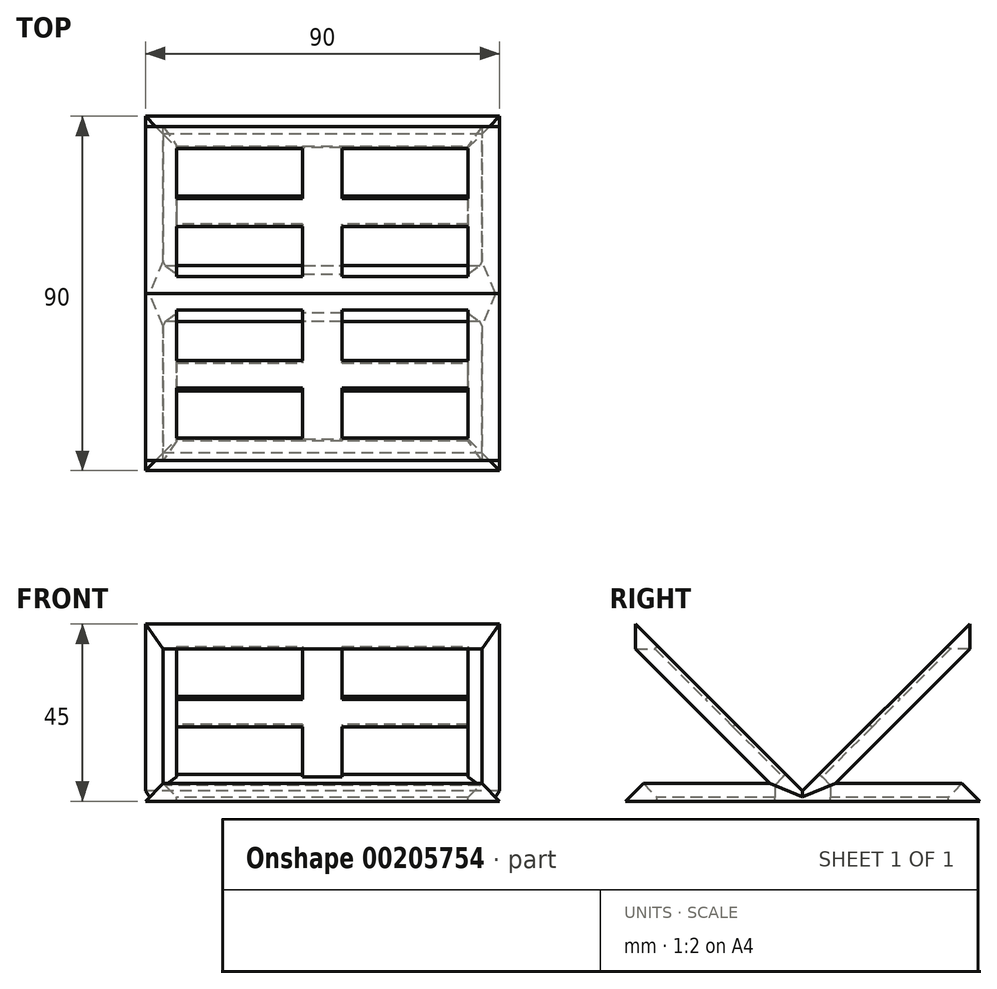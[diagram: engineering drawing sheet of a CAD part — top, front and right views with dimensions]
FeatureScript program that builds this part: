
annotation { "Feature Type Name" : "Feature", "Feature Type Description" : "" }
export const myFeature = defineFeature(function(context is Context, id is Id, definition is map)
    precondition{}
    {
        {
            var Q0;
            Q0=qCreatedBy(makeId("Right.planeOp"),FACE);
            var sketch = newSketch(context, id + "F12", { "sketchPlane" : qUnion([Q0])});
            skLineSegment(sketch, "E0.bottom", {"start": v(-45, 45) * mm, "end": v(45, 45) * mm});
            skLineSegment(sketch, "E0.top", {"start": v(-45, 0) * mm, "end": v(45, 0) * mm});
            skLineSegment(sketch, "E0.left", {"start": v(-45, 45) * mm, "end": v(-45, 0) * mm});
            skLineSegment(sketch, "E0.right", {"start": v(45, 45) * mm, "end": v(45, 0) * mm});
            skLineSegment(sketch, "E1", {"start": v(-42.43, 45) * mm, "end": v(0, 2.57) * mm});
            skLineSegment(sketch, "E2", {"start": v(0, 0) * mm, "end": v(0, 45) * mm, "construction": true});
            skLineSegment(sketch, "E3.MirrorCS", {"start": v(42.43, 45) * mm, "end": v(0, 2.57) * mm});
            skSolve(sketch);
        }
        {
            var Q0;
            Q0=makeQuery(id+"F12.imprint","IMPRINT",FACE,{"disambiguationData":[TD([[makeQuery(id+"F12.imprint","IMPRINT",EDGE,{"derivedFrom":sQuery(id+"F12.wireOp",EDGE,"E0.top")}),1.0]])]});
            extrude(context, id + "F0", {"entities" : qUnion([Q0]), "depth" : 45 * mm});
        }
        {
            var Q0;
            Q0=makeQuery(id+"F0.opExtrude","SWEPT_BODY",BODY,{"disambiguationData":[OSD([sQuery(id+"F12.wireOp",EDGE,"E0.bottom"),sQuery(id+"F12.wireOp",EDGE,"E0.top"),sQuery(id+"F12.wireOp",EDGE,"E0.left"),sQuery(id+"F12.wireOp",EDGE,"E0.right"),sQuery(id+"F12.wireOp",EDGE,"E1"),sQuery(id+"F12.wireOp",EDGE,"E3.MirrorCS")])]});
            var Q1;
            Q1=qCreatedBy(makeId("Right.planeOp"),FACE);
            mirror(context, id + "F1", {"operationType" : NewBodyOperationType.ADD, "entities" : qUnion([Q0]), "mirrorPlane" : qUnion([Q1])});
        }
        {
            var Q0;
            {var subQ0=makeQuery(id+"F0.opExtrude","SWEPT_FACE",FACE,{"disambiguationData":[OSD([sQuery(id+"F12.wireOp",EDGE,"E0.left")])]});Q0=makeQuery(id+"F1.boolean.opBoolean","MERGE",FACE,{"derivedFrom":[subQ0,makeQuery(id+"F1.opPattern","COPY",FACE,{"derivedFrom":subQ0,"instanceName":"1"})]});}
            var Q1;
            {var subQ0=makeQuery(id+"F0.opExtrude","SWEPT_FACE",FACE,{"disambiguationData":[OSD([sQuery(id+"F12.wireOp",EDGE,"E0.right")])]});Q1=makeQuery(id+"F1.boolean.opBoolean","MERGE",FACE,{"derivedFrom":[subQ0,makeQuery(id+"F1.opPattern","COPY",FACE,{"derivedFrom":subQ0,"instanceName":"1"})]});}
            var Q2;
            Q2=makeQuery(id+"F1.opPattern","COPY",FACE,{"derivedFrom":makeQuery(id+"F0.opExtrude","CAP_FACE",FACE,{"disambiguationData":[OSD([sQuery(id+"F12.wireOp",EDGE,"E0.bottom"),sQuery(id+"F12.wireOp",EDGE,"E0.top"),sQuery(id+"F12.wireOp",EDGE,"E0.left"),sQuery(id+"F12.wireOp",EDGE,"E0.right"),sQuery(id+"F12.wireOp",EDGE,"E1"),sQuery(id+"F12.wireOp",EDGE,"E3.MirrorCS")])],"isStart":false}),"instanceName":"1"});
            var Q3;
            Q3=makeQuery(id+"F0.opExtrude","CAP_FACE",FACE,{"disambiguationData":[OSD([sQuery(id+"F12.wireOp",EDGE,"E0.bottom"),sQuery(id+"F12.wireOp",EDGE,"E0.top"),sQuery(id+"F12.wireOp",EDGE,"E0.left"),sQuery(id+"F12.wireOp",EDGE,"E0.right"),sQuery(id+"F12.wireOp",EDGE,"E1"),sQuery(id+"F12.wireOp",EDGE,"E3.MirrorCS")])],"isStart":false});
            shell(context, id + "F2", {"entities" : qUnion([Q0, Q1, Q2, Q3]), "thickness" : 4 * mm});
        }
        {
            var Q0;
            {var subQ0=sQuery(id+"F12.wireOp",EDGE,"E0.bottom");var subQ1=makeQuery(id+"F0.opExtrude","SWEPT_FACE",FACE,{"disambiguationData":[OSD([subQ0]),TDD([makeQuery(id+"F12.imprint","IMPRINT",EDGE,{"disambiguationData":[TD([[makeQuery(id+"F12.imprint","INTERSECT",VERTEX,{"derivedFrom":[subQ0,sQuery(id+"F12.wireOp",EDGE,"E0.right")]}),1.0]])],"derivedFrom":subQ0})])]});Q0=makeQuery(id+"F1.boolean.opBoolean","MERGE",FACE,{"derivedFrom":[subQ1,makeQuery(id+"F1.opPattern","COPY",FACE,{"derivedFrom":subQ1,"instanceName":"1"})]});}
            extrude(context, id + "F13", {"entities" : qUnion([Q0]), "operationType" : NewBodyOperationType.REMOVE, "oppositeDirection" : true, "depth" : 17.8 * mm});
        }
        {
            var Q0;
            {var subQ0=sQuery(id+"F12.wireOp",EDGE,"E0.bottom");var subQ1=makeQuery(id+"F0.opExtrude","SWEPT_FACE",FACE,{"disambiguationData":[OSD([subQ0]),TDD([makeQuery(id+"F12.imprint","IMPRINT",EDGE,{"disambiguationData":[TD([[makeQuery(id+"F12.imprint","INTERSECT",VERTEX,{"derivedFrom":[subQ0,sQuery(id+"F12.wireOp",EDGE,"E0.left")]}),-1.0]])],"derivedFrom":subQ0})])]});Q0=makeQuery(id+"F1.boolean.opBoolean","MERGE",FACE,{"derivedFrom":[subQ1,makeQuery(id+"F1.opPattern","COPY",FACE,{"derivedFrom":subQ1,"instanceName":"1"})]});}
            extrude(context, id + "F3", {"entities" : qUnion([Q0]), "operationType" : NewBodyOperationType.REMOVE, "oppositeDirection" : true, "depth" : 25 * mm});
        }
        {
            var Q0;
            Q0=makeQuery(id+"F0.opExtrude","CAP_FACE",FACE,{"disambiguationData":[OSD([sQuery(id+"F12.wireOp",EDGE,"E0.bottom"),sQuery(id+"F12.wireOp",EDGE,"E0.top"),sQuery(id+"F12.wireOp",EDGE,"E0.left"),sQuery(id+"F12.wireOp",EDGE,"E0.right"),sQuery(id+"F12.wireOp",EDGE,"E1"),sQuery(id+"F12.wireOp",EDGE,"E3.MirrorCS")])],"isStart":false});
            var sketch = newSketch(context, id + "F14", { "sketchPlane" : qUnion([Q0])});
            skLineSegment(sketch, "E4", {"start": v(-45, 0) * mm, "end": v(-41, 4) * mm});
            skLineSegment(sketch, "E5", {"start": v(-41, 4) * mm, "end": v(-45, 4) * mm});
            skLineSegment(sketch, "E6", {"start": v(-45, 4) * mm, "end": v(-45, 0) * mm});
            skLineSegment(sketch, "E7", {"start": v(41, 4) * mm, "end": v(45, 0) * mm});
            skLineSegment(sketch, "E8", {"start": v(41, 4) * mm, "end": v(45, 4) * mm});
            skLineSegment(sketch, "E9", {"start": v(45, 4) * mm, "end": v(45, 4) * mm});
            skLineSegment(sketch, "E10", {"start": v(45, 0) * mm, "end": v(45, 4) * mm});
            skSolve(sketch);
        }
        {
            var Q0;
            Q0 = qSketchRegion(id + "F14", true);
            extrude(context, id + "F15", {"entities" : qUnion([Q0]), "operationType" : NewBodyOperationType.REMOVE, "endBound" : BoundingType.THROUGH_ALL, "oppositeDirection" : true, "depth" : 25 * mm});
        }
        {
            var Q0;
            {var subQ0=sQuery(id+"F12.wireOp",EDGE,"E1");Q0=makeQuery(id+"F2.opShell","OFFSET_EDGE",EDGE,{"disambiguationData":[OSD([subQ0]),TDD([makeQuery(id+"F0.opExtrude","CAP_EDGE",EDGE,{"disambiguationData":[OSD([subQ0])],"isStart":false})])]});}
            var Q1;
            {var subQ0=sQuery(id+"F12.wireOp",EDGE,"E1");Q1=makeQuery(id+"F2.opShell","OFFSET_EDGE",EDGE,{"disambiguationData":[OSD([subQ0]),TDD([makeQuery(id+"F1.opPattern","COPY",EDGE,{"derivedFrom":makeQuery(id+"F0.opExtrude","CAP_EDGE",EDGE,{"disambiguationData":[OSD([subQ0])],"isStart":false}),"instanceName":"1"})])]});}
            var Q2;
            {var subQ0=sQuery(id+"F12.wireOp",EDGE,"E0.top");Q2=makeQuery(id+"F2.opShell","OFFSET_EDGE",EDGE,{"disambiguationData":[OSD([subQ0]),TDD([makeQuery(id+"F1.opPattern","COPY",EDGE,{"derivedFrom":makeQuery(id+"F0.opExtrude","CAP_EDGE",EDGE,{"disambiguationData":[OSD([subQ0])],"isStart":false}),"instanceName":"1"})]),OD(0.0)]});}
            var Q3;
            {var subQ0=sQuery(id+"F12.wireOp",EDGE,"E0.top");Q3=makeQuery(id+"F2.opShell","OFFSET_EDGE",EDGE,{"disambiguationData":[OSD([subQ0]),TDD([makeQuery(id+"F0.opExtrude","CAP_EDGE",EDGE,{"disambiguationData":[OSD([subQ0])],"isStart":false})]),OD(0.0)]});}
            var Q4;
            {var subQ0=sQuery(id+"F12.wireOp",EDGE,"E0.top");Q4=makeQuery(id+"F2.opShell","OFFSET_EDGE",EDGE,{"disambiguationData":[OSD([subQ0]),TDD([makeQuery(id+"F0.opExtrude","CAP_EDGE",EDGE,{"disambiguationData":[OSD([subQ0])],"isStart":false})]),OD(1.0)]});}
            var Q5;
            {var subQ0=sQuery(id+"F12.wireOp",EDGE,"E0.top");Q5=makeQuery(id+"F2.opShell","OFFSET_EDGE",EDGE,{"disambiguationData":[OSD([subQ0]),TDD([makeQuery(id+"F1.opPattern","COPY",EDGE,{"derivedFrom":makeQuery(id+"F0.opExtrude","CAP_EDGE",EDGE,{"disambiguationData":[OSD([subQ0])],"isStart":false}),"instanceName":"1"})]),OD(1.0)]});}
            var Q6;
            {var subQ0=sQuery(id+"F12.wireOp",EDGE,"E3.MirrorCS");Q6=makeQuery(id+"F2.opShell","OFFSET_EDGE",EDGE,{"disambiguationData":[OSD([subQ0]),TDD([makeQuery(id+"F1.opPattern","COPY",EDGE,{"derivedFrom":makeQuery(id+"F0.opExtrude","CAP_EDGE",EDGE,{"disambiguationData":[OSD([subQ0])],"isStart":false}),"instanceName":"1"})])]});}
            var Q7;
            {var subQ0=sQuery(id+"F12.wireOp",EDGE,"E3.MirrorCS");Q7=makeQuery(id+"F2.opShell","OFFSET_EDGE",EDGE,{"disambiguationData":[OSD([subQ0]),TDD([makeQuery(id+"F0.opExtrude","CAP_EDGE",EDGE,{"disambiguationData":[OSD([subQ0])],"isStart":false})])]});}
            chamfer(context, id + "F4", {"entities" : qUnion([Q0, Q1, Q2, Q3, Q4, Q5, Q6, Q7]), "width" : 4 * mm, "tangentPropagation" : true});
        }
        {
            var Q0;
            Q0=makeQuery(id+"F2.opShell","OFFSET_FACE",FACE,{"disambiguationData":[OSD([sQuery(id+"F12.wireOp",EDGE,"E0.top")]),OD(0.0)]});
            extrude(context, id + "F5", {"entities" : qUnion([Q0]), "operationType" : NewBodyOperationType.REMOVE, "oppositeDirection" : true, "depth" : 3 * mm});
        }
        {
            var Q0;
            Q0=makeQuery(id+"F2.opShell","OFFSET_FACE",FACE,{"disambiguationData":[OSD([sQuery(id+"F12.wireOp",EDGE,"E0.top")]),OD(1.0)]});
            extrude(context, id + "F16", {"entities" : qUnion([Q0]), "operationType" : NewBodyOperationType.REMOVE, "oppositeDirection" : true, "depth" : 3 * mm});
        }
        {
            var Q0;
            Q0=makeQuery(id+"F2.opShell","OFFSET_FACE",FACE,{"disambiguationData":[OSD([sQuery(id+"F12.wireOp",EDGE,"E3.MirrorCS")])]});
            extrude(context, id + "F17", {"entities" : qUnion([Q0]), "operationType" : NewBodyOperationType.REMOVE, "oppositeDirection" : true, "depth" : 3 * mm});
        }
        {
            var Q0;
            Q0=makeQuery(id+"F2.opShell","OFFSET_FACE",FACE,{"disambiguationData":[OSD([sQuery(id+"F12.wireOp",EDGE,"E1")])]});
            extrude(context, id + "F6", {"entities" : qUnion([Q0]), "operationType" : NewBodyOperationType.REMOVE, "oppositeDirection" : true, "depth" : 3 * mm});
        }
        {
            var Q0;
            {var subQ0=sQuery(id+"F12.wireOp",EDGE,"E3.MirrorCS");Q0=makeQuery(id+"F17.boolean.opBoolean","COPY",EDGE,{"derivedFrom":makeQuery(id+"F17.opExtrude","CAP_EDGE",EDGE,{"disambiguationData":[OSD([subQ0]),TDD([makeQuery(id+"F4.opChamfer","BLEND_EDGE",EDGE,{"blendedFrom":[makeQuery(id+"F2.opShell","OFFSET_EDGE",EDGE,{"disambiguationData":[OSD([subQ0]),TDD([makeQuery(id+"F0.opExtrude","CAP_EDGE",EDGE,{"disambiguationData":[OSD([subQ0])],"isStart":false})])]}),makeQuery(id+"F2.opShell","OFFSET_FACE",FACE,{"disambiguationData":[OSD([subQ0])]})],"blendedInto":[makeQuery(id+"F2.opShell","OFFSET_FACE",FACE,{"disambiguationData":[OSD([subQ0])]})]})])],"isStart":false})});}
            var Q1;
            {var subQ0=sQuery(id+"F12.wireOp",EDGE,"E3.MirrorCS");Q1=makeQuery(id+"F17.boolean.opBoolean","COPY",EDGE,{"derivedFrom":makeQuery(id+"F17.opExtrude","CAP_EDGE",EDGE,{"disambiguationData":[OSD([subQ0]),TDD([makeQuery(id+"F4.opChamfer","BLEND_EDGE",EDGE,{"blendedFrom":[makeQuery(id+"F2.opShell","OFFSET_EDGE",EDGE,{"disambiguationData":[OSD([subQ0]),TDD([makeQuery(id+"F1.opPattern","COPY",EDGE,{"derivedFrom":makeQuery(id+"F0.opExtrude","CAP_EDGE",EDGE,{"disambiguationData":[OSD([subQ0])],"isStart":false}),"instanceName":"1"})])]}),makeQuery(id+"F2.opShell","OFFSET_FACE",FACE,{"disambiguationData":[OSD([subQ0])]})],"blendedInto":[makeQuery(id+"F2.opShell","OFFSET_FACE",FACE,{"disambiguationData":[OSD([subQ0])]})]})])],"isStart":false})});}
            var Q2;
            Q2=makeQuery(id+"F17.boolean.opBoolean","COPY",EDGE,{"derivedFrom":makeQuery(id+"F17.opExtrude","CAP_EDGE",EDGE,{"disambiguationData":[OSD([sQuery(id+"F12.wireOp",EDGE,"E0.bottom"),sQuery(id+"F12.wireOp",EDGE,"E3.MirrorCS")])],"isStart":false})});
            var Q3;
            {var subQ0=sQuery(id+"F12.wireOp",EDGE,"E1");Q3=makeQuery(id+"F6.boolean.opBoolean","COPY",EDGE,{"derivedFrom":makeQuery(id+"F6.opExtrude","CAP_EDGE",EDGE,{"disambiguationData":[OSD([subQ0]),TDD([makeQuery(id+"F4.opChamfer","BLEND_EDGE",EDGE,{"blendedFrom":[makeQuery(id+"F2.opShell","OFFSET_EDGE",EDGE,{"disambiguationData":[OSD([subQ0]),TDD([makeQuery(id+"F1.opPattern","COPY",EDGE,{"derivedFrom":makeQuery(id+"F0.opExtrude","CAP_EDGE",EDGE,{"disambiguationData":[OSD([subQ0])],"isStart":false}),"instanceName":"1"})])]}),makeQuery(id+"F2.opShell","OFFSET_FACE",FACE,{"disambiguationData":[OSD([subQ0])]})],"blendedInto":[makeQuery(id+"F2.opShell","OFFSET_FACE",FACE,{"disambiguationData":[OSD([subQ0])]})]})])],"isStart":false})});}
            var Q4;
            Q4=makeQuery(id+"F6.boolean.opBoolean","COPY",EDGE,{"derivedFrom":makeQuery(id+"F6.opExtrude","CAP_EDGE",EDGE,{"disambiguationData":[OSD([sQuery(id+"F12.wireOp",EDGE,"E0.bottom"),sQuery(id+"F12.wireOp",EDGE,"E1")])],"isStart":false})});
            var Q5;
            {var subQ0=sQuery(id+"F12.wireOp",EDGE,"E1");Q5=makeQuery(id+"F6.boolean.opBoolean","COPY",EDGE,{"derivedFrom":makeQuery(id+"F6.opExtrude","CAP_EDGE",EDGE,{"disambiguationData":[OSD([subQ0]),TDD([makeQuery(id+"F4.opChamfer","BLEND_EDGE",EDGE,{"blendedFrom":[makeQuery(id+"F2.opShell","OFFSET_EDGE",EDGE,{"disambiguationData":[OSD([subQ0]),TDD([makeQuery(id+"F0.opExtrude","CAP_EDGE",EDGE,{"disambiguationData":[OSD([subQ0])],"isStart":false})])]}),makeQuery(id+"F2.opShell","OFFSET_FACE",FACE,{"disambiguationData":[OSD([subQ0])]})],"blendedInto":[makeQuery(id+"F2.opShell","OFFSET_FACE",FACE,{"disambiguationData":[OSD([subQ0])]})]})])],"isStart":false})});}
            chamfer(context, id + "F18", {"entities" : qUnion([Q0, Q1, Q2, Q3, Q4, Q5]), "width" : 4 * mm, "tangentPropagation" : true});
        }
        {
            var Q0;
            {var subQ0=sQuery(id+"F12.wireOp",EDGE,"E0.top");Q0=makeQuery(id+"F16.boolean.opBoolean","COPY",EDGE,{"derivedFrom":makeQuery(id+"F16.opExtrude","CAP_EDGE",EDGE,{"disambiguationData":[OSD([subQ0]),TDD([makeQuery(id+"F4.opChamfer","BLEND_EDGE",EDGE,{"blendedFrom":[makeQuery(id+"F2.opShell","OFFSET_EDGE",EDGE,{"disambiguationData":[OSD([subQ0]),TDD([makeQuery(id+"F0.opExtrude","CAP_EDGE",EDGE,{"disambiguationData":[OSD([subQ0])],"isStart":false})]),OD(1.0)]}),makeQuery(id+"F2.opShell","OFFSET_FACE",FACE,{"disambiguationData":[OSD([subQ0]),OD(1.0)]})],"blendedInto":[makeQuery(id+"F2.opShell","OFFSET_FACE",FACE,{"disambiguationData":[OSD([subQ0]),OD(1.0)]})]})])],"isStart":false})});}
            var Q1;
            Q1=makeQuery(id+"F16.boolean.opBoolean","COPY",EDGE,{"derivedFrom":makeQuery(id+"F16.opExtrude","CAP_EDGE",EDGE,{"disambiguationData":[OSD([sQuery(id+"F12.wireOp",EDGE,"E0.top"),sQuery(id+"F14.wireOp",EDGE,"E7"),sQuery(id+"F14.wireOp",EDGE,"E8")])],"isStart":false})});
            var Q2;
            {var subQ0=sQuery(id+"F12.wireOp",EDGE,"E0.top");Q2=makeQuery(id+"F16.boolean.opBoolean","COPY",EDGE,{"derivedFrom":makeQuery(id+"F16.opExtrude","CAP_EDGE",EDGE,{"disambiguationData":[OSD([subQ0]),TDD([makeQuery(id+"F4.opChamfer","BLEND_EDGE",EDGE,{"blendedFrom":[makeQuery(id+"F2.opShell","OFFSET_EDGE",EDGE,{"disambiguationData":[OSD([subQ0]),TDD([makeQuery(id+"F1.opPattern","COPY",EDGE,{"derivedFrom":makeQuery(id+"F0.opExtrude","CAP_EDGE",EDGE,{"disambiguationData":[OSD([subQ0])],"isStart":false}),"instanceName":"1"})]),OD(1.0)]}),makeQuery(id+"F2.opShell","OFFSET_FACE",FACE,{"disambiguationData":[OSD([subQ0]),OD(1.0)]})],"blendedInto":[makeQuery(id+"F2.opShell","OFFSET_FACE",FACE,{"disambiguationData":[OSD([subQ0]),OD(1.0)]})]})])],"isStart":false})});}
            var Q3;
            {var subQ0=sQuery(id+"F12.wireOp",EDGE,"E0.top");Q3=makeQuery(id+"F5.boolean.opBoolean","COPY",EDGE,{"derivedFrom":makeQuery(id+"F5.opExtrude","CAP_EDGE",EDGE,{"disambiguationData":[OSD([subQ0]),TDD([makeQuery(id+"F4.opChamfer","BLEND_EDGE",EDGE,{"blendedFrom":[makeQuery(id+"F2.opShell","OFFSET_EDGE",EDGE,{"disambiguationData":[OSD([subQ0]),TDD([makeQuery(id+"F0.opExtrude","CAP_EDGE",EDGE,{"disambiguationData":[OSD([subQ0])],"isStart":false})]),OD(0.0)]}),makeQuery(id+"F2.opShell","OFFSET_FACE",FACE,{"disambiguationData":[OSD([subQ0]),OD(0.0)]})],"blendedInto":[makeQuery(id+"F2.opShell","OFFSET_FACE",FACE,{"disambiguationData":[OSD([subQ0]),OD(0.0)]})]})])],"isStart":false})});}
            var Q4;
            {var subQ0=sQuery(id+"F12.wireOp",EDGE,"E0.top");Q4=makeQuery(id+"F5.boolean.opBoolean","COPY",EDGE,{"derivedFrom":makeQuery(id+"F5.opExtrude","CAP_EDGE",EDGE,{"disambiguationData":[OSD([subQ0]),TDD([makeQuery(id+"F4.opChamfer","BLEND_EDGE",EDGE,{"blendedFrom":[makeQuery(id+"F2.opShell","OFFSET_EDGE",EDGE,{"disambiguationData":[OSD([subQ0]),TDD([makeQuery(id+"F1.opPattern","COPY",EDGE,{"derivedFrom":makeQuery(id+"F0.opExtrude","CAP_EDGE",EDGE,{"disambiguationData":[OSD([subQ0])],"isStart":false}),"instanceName":"1"})]),OD(0.0)]}),makeQuery(id+"F2.opShell","OFFSET_FACE",FACE,{"disambiguationData":[OSD([subQ0]),OD(0.0)]})],"blendedInto":[makeQuery(id+"F2.opShell","OFFSET_FACE",FACE,{"disambiguationData":[OSD([subQ0]),OD(0.0)]})]})])],"isStart":false})});}
            var Q5;
            Q5=makeQuery(id+"F5.boolean.opBoolean","COPY",EDGE,{"derivedFrom":makeQuery(id+"F5.opExtrude","CAP_EDGE",EDGE,{"disambiguationData":[OSD([sQuery(id+"F12.wireOp",EDGE,"E0.top"),sQuery(id+"F14.wireOp",EDGE,"E4"),sQuery(id+"F14.wireOp",EDGE,"E5")])],"isStart":false})});
            chamfer(context, id + "F7", {"entities" : qUnion([Q0, Q1, Q2, Q3, Q4, Q5]), "width" : 4 * mm, "tangentPropagation" : true});
        }
        {
            var Q0;
            Q0=makeQuery(id+"F5.boolean.opBoolean","COPY",FACE,{"derivedFrom":makeQuery(id+"F5.opExtrude","CAP_FACE",FACE,{"disambiguationData":[OSD([sQuery(id+"F12.wireOp",EDGE,"E0.top")])],"isStart":false})});
            extrude(context, id + "F8", {"entities" : qUnion([Q0]), "operationType" : NewBodyOperationType.REMOVE, "oppositeDirection" : true, "depth" : 84.27 * mm});
        }
        {
            var Q0;
            Q0=makeQuery(id+"F16.boolean.opBoolean","COPY",FACE,{"derivedFrom":makeQuery(id+"F16.opExtrude","CAP_FACE",FACE,{"disambiguationData":[OSD([sQuery(id+"F12.wireOp",EDGE,"E0.top")])],"isStart":false})});
            extrude(context, id + "F9", {"entities" : qUnion([Q0]), "operationType" : NewBodyOperationType.REMOVE, "oppositeDirection" : true, "depth" : 25 * mm});
        }
        {
            var Q0;
            Q0=makeQuery(id+"F17.boolean.opBoolean","COPY",FACE,{"derivedFrom":makeQuery(id+"F17.opExtrude","CAP_FACE",FACE,{"disambiguationData":[OSD([sQuery(id+"F12.wireOp",EDGE,"E3.MirrorCS")])],"isStart":false})});
            var sketch = newSketch(context, id + "F10", { "sketchPlane" : qUnion([Q0])});
            skLineSegment(sketch, "E11.bottom", {"start": v(-5, 53.82) * mm, "end": v(5, 53.82) * mm});
            skLineSegment(sketch, "E11.top", {"start": v(-5, 7.84) * mm, "end": v(5, 7.84) * mm});
            skLineSegment(sketch, "E11.left", {"start": v(-5, 53.82) * mm, "end": v(-5, 7.84) * mm});
            skLineSegment(sketch, "E11.right", {"start": v(5, 53.82) * mm, "end": v(5, 7.84) * mm});
            skLineSegment(sketch, "E12.bottom", {"start": v(-37, 35.83) * mm, "end": v(37, 35.83) * mm});
            skLineSegment(sketch, "E12.top", {"start": v(-37, 25.83) * mm, "end": v(37, 25.83) * mm});
            skLineSegment(sketch, "E12.left", {"start": v(-37, 35.83) * mm, "end": v(-37, 25.83) * mm});
            skLineSegment(sketch, "E12.right", {"start": v(37, 35.83) * mm, "end": v(37, 25.83) * mm});
            skLineSegment(sketch, "E13", {"start": v(5, 7.84) * mm, "end": v(0, 0) * mm, "construction": true});
            skLineSegment(sketch, "E14", {"start": v(-5, 7.84) * mm, "end": v(0, 0) * mm, "construction": true});
            skLineSegment(sketch, "E15", {"start": v(37, 35.83) * mm, "end": v(37, 53.82) * mm, "construction": true});
            skLineSegment(sketch, "E16", {"start": v(37, 25.83) * mm, "end": v(37, 7.84) * mm, "construction": true});
            skLineSegment(sketch, "E17.bottom", {"start": v(-37, 53.82) * mm, "end": v(37, 53.82) * mm});
            skLineSegment(sketch, "E17.top", {"start": v(-37, 7.84) * mm, "end": v(37, 7.84) * mm});
            skLineSegment(sketch, "E17.left", {"start": v(-37, 53.82) * mm, "end": v(-37, 7.84) * mm});
            skLineSegment(sketch, "E17.right", {"start": v(37, 53.82) * mm, "end": v(37, 7.84) * mm});
            skSolve(sketch);
        }
        {
            var Q0;
            {var subQ0=sQuery(id+"F10.wireOp",EDGE,"E17.top");var subQ1=sQuery(id+"F10.wireOp",EDGE,"E11.right");var subQ2=makeQuery(id+"F10.imprint","INTERSECT",VERTEX,{"derivedFrom":[subQ1,subQ0]});Q0=makeQuery(id+"F10.imprint","IMPRINT",FACE,{"disambiguationData":[TD([[makeQuery(id+"F10.imprint","IMPRINT",EDGE,{"disambiguationData":[TD([[subQ2,1.0]])],"derivedFrom":subQ1}),1.0]])]});}
            var Q1;
            {var subQ0=sQuery(id+"F10.wireOp",EDGE,"E17.top");var subQ1=sQuery(id+"F10.wireOp",EDGE,"E11.left");var subQ2=makeQuery(id+"F10.imprint","INTERSECT",VERTEX,{"derivedFrom":[subQ1,subQ0]});Q1=makeQuery(id+"F10.imprint","IMPRINT",FACE,{"disambiguationData":[TD([[makeQuery(id+"F10.imprint","IMPRINT",EDGE,{"disambiguationData":[TD([[subQ2,1.0]])],"derivedFrom":subQ1}),-1.0]])]});}
            var Q2;
            {var subQ0=sQuery(id+"F10.wireOp",EDGE,"E17.bottom");var subQ1=sQuery(id+"F10.wireOp",EDGE,"E11.right");var subQ2=makeQuery(id+"F10.imprint","INTERSECT",VERTEX,{"derivedFrom":[subQ1,subQ0]});Q2=makeQuery(id+"F10.imprint","IMPRINT",FACE,{"disambiguationData":[TD([[makeQuery(id+"F10.imprint","IMPRINT",EDGE,{"disambiguationData":[TD([[subQ2,-1.0]])],"derivedFrom":subQ1}),1.0]])]});}
            var Q3;
            {var subQ0=sQuery(id+"F10.wireOp",EDGE,"E17.bottom");var subQ1=sQuery(id+"F10.wireOp",EDGE,"E11.left");var subQ2=makeQuery(id+"F10.imprint","INTERSECT",VERTEX,{"derivedFrom":[subQ1,subQ0]});Q3=makeQuery(id+"F10.imprint","IMPRINT",FACE,{"disambiguationData":[TD([[makeQuery(id+"F10.imprint","IMPRINT",EDGE,{"disambiguationData":[TD([[subQ2,-1.0]])],"derivedFrom":subQ1}),-1.0]])]});}
            extrude(context, id + "F11", {"entities" : qUnion([Q0, Q1, Q2, Q3]), "operationType" : NewBodyOperationType.REMOVE, "oppositeDirection" : true, "depth" : 25 * mm});
        }
        {
            var Q0;
            Q0=makeQuery(id+"F6.boolean.opBoolean","COPY",FACE,{"derivedFrom":makeQuery(id+"F6.opExtrude","CAP_FACE",FACE,{"disambiguationData":[OSD([sQuery(id+"F12.wireOp",EDGE,"E1")])],"isStart":false})});
            var sketch = newSketch(context, id + "F19", { "sketchPlane" : qUnion([Q0])});
            skLineSegment(sketch, "E18.bottom", {"start": v(-5, 53.82) * mm, "end": v(5, 53.82) * mm});
            skLineSegment(sketch, "E18.top", {"start": v(-5, 7.84) * mm, "end": v(5, 7.84) * mm});
            skLineSegment(sketch, "E18.left", {"start": v(-5, 53.82) * mm, "end": v(-5, 7.84) * mm});
            skLineSegment(sketch, "E18.right", {"start": v(5, 53.82) * mm, "end": v(5, 7.84) * mm});
            skLineSegment(sketch, "E19.bottom", {"start": v(-37, 35.83) * mm, "end": v(37, 35.83) * mm});
            skLineSegment(sketch, "E19.top", {"start": v(-37, 25.83) * mm, "end": v(37, 25.83) * mm});
            skLineSegment(sketch, "E19.left", {"start": v(-37, 35.83) * mm, "end": v(-37, 25.83) * mm});
            skLineSegment(sketch, "E19.right", {"start": v(37, 35.83) * mm, "end": v(37, 25.83) * mm});
            skLineSegment(sketch, "E20.bottom", {"start": v(-37, 53.82) * mm, "end": v(37, 53.82) * mm});
            skLineSegment(sketch, "E20.top", {"start": v(-37, 7.84) * mm, "end": v(37, 7.84) * mm});
            skLineSegment(sketch, "E20.left", {"start": v(-37, 53.82) * mm, "end": v(-37, 7.84) * mm});
            skLineSegment(sketch, "E20.right", {"start": v(37, 53.82) * mm, "end": v(37, 7.84) * mm});
            skLineSegment(sketch, "E21", {"start": v(37, 35.83) * mm, "end": v(37, 53.82) * mm, "construction": true});
            skLineSegment(sketch, "E22", {"start": v(37, 25.83) * mm, "end": v(37, 7.84) * mm, "construction": true});
            skLineSegment(sketch, "E23", {"start": v(-5, 7.84) * mm, "end": v(0, 0) * mm, "construction": true});
            skLineSegment(sketch, "E24", {"start": v(0, 0) * mm, "end": v(0, 0) * mm});
            skLineSegment(sketch, "E25", {"start": v(5, 7.84) * mm, "end": v(0, 0) * mm, "construction": true});
            skSolve(sketch);
        }
        {
            var Q0;
            {var subQ0=sQuery(id+"F19.wireOp",EDGE,"E20.bottom");var subQ1=sQuery(id+"F19.wireOp",EDGE,"E18.left");var subQ2=makeQuery(id+"F19.imprint","INTERSECT",VERTEX,{"derivedFrom":[subQ1,subQ0]});Q0=makeQuery(id+"F19.imprint","IMPRINT",FACE,{"disambiguationData":[TD([[makeQuery(id+"F19.imprint","IMPRINT",EDGE,{"disambiguationData":[TD([[subQ2,-1.0]])],"derivedFrom":subQ1}),-1.0]])]});}
            var Q1;
            {var subQ0=sQuery(id+"F19.wireOp",EDGE,"E20.top");var subQ1=sQuery(id+"F19.wireOp",EDGE,"E18.right");var subQ2=makeQuery(id+"F19.imprint","INTERSECT",VERTEX,{"derivedFrom":[subQ1,subQ0]});Q1=makeQuery(id+"F19.imprint","IMPRINT",FACE,{"disambiguationData":[TD([[makeQuery(id+"F19.imprint","IMPRINT",EDGE,{"disambiguationData":[TD([[subQ2,1.0]])],"derivedFrom":subQ1}),1.0]])]});}
            var Q2;
            {var subQ0=sQuery(id+"F19.wireOp",EDGE,"E20.top");var subQ1=sQuery(id+"F19.wireOp",EDGE,"E18.left");var subQ2=makeQuery(id+"F19.imprint","INTERSECT",VERTEX,{"derivedFrom":[subQ1,subQ0]});Q2=makeQuery(id+"F19.imprint","IMPRINT",FACE,{"disambiguationData":[TD([[makeQuery(id+"F19.imprint","IMPRINT",EDGE,{"disambiguationData":[TD([[subQ2,1.0]])],"derivedFrom":subQ1}),-1.0]])]});}
            var Q3;
            {var subQ0=sQuery(id+"F19.wireOp",EDGE,"E20.bottom");var subQ1=sQuery(id+"F19.wireOp",EDGE,"E18.right");var subQ2=makeQuery(id+"F19.imprint","INTERSECT",VERTEX,{"derivedFrom":[subQ1,subQ0]});Q3=makeQuery(id+"F19.imprint","IMPRINT",FACE,{"disambiguationData":[TD([[makeQuery(id+"F19.imprint","IMPRINT",EDGE,{"disambiguationData":[TD([[subQ2,-1.0]])],"derivedFrom":subQ1}),1.0]])]});}
            extrude(context, id + "F20", {"entities" : qUnion([Q0, Q1, Q2, Q3]), "operationType" : NewBodyOperationType.REMOVE, "oppositeDirection" : true, "depth" : 25 * mm});
        }
    });
